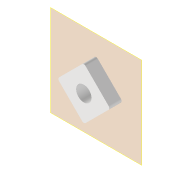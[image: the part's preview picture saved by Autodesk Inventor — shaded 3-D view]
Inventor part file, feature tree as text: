
AUTODESK INVENTOR PART (.ipt)
format: ipt  version: 2022 (Build 260153000, 153)  size: 101,888 bytes
history: native  units: mm
features: other x2, plane x1, extrude x1, sketch x1, reference x1
ambient origin geometry x8: Origin, YZ Plane, XZ Plane, XY Plane, X Axis, Y Axis, Z Axis, Center Point
bodies: Volumenkörper1 (feature_tree)
feature tree (6):
  plane  "Arbeitsebene1"
  extrude  "Extrusion1"  Depth=10.0mm
  sketch  "Skizze1"  dims[d0=0.5mm d1=10.0mm d2=8.0mm d3=0.0mm]
  reference  "Referenz1"
  other  "Assembly_Matchboxscope_injectionmolded.iam"
  other  "IM_Matchboxscope_plate:2"
